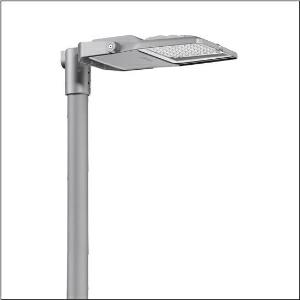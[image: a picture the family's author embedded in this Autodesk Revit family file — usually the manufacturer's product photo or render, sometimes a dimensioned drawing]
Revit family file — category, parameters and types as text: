
# Revit family: floodlight_fl_21_iq_mini___pl52_5xa7771d4d3a_bc98
name_source: partatom
category: Lighting Fixtures
units: mm (PartAtom-declared; Revit-internal decimal feet)

## family parameters
Cut with Voids When Loaded = No
Host = Face
Light Source = No
Part Type = Normal
Room Calculation Point = No
Round Connector Dimension = Use Diameter
Shared = No

## types (1)
- --- (1 x LED, 18610 lm, 143 W, 4000K)
    Apparent Load = 143 VA
    CIE Flux Codes = 26 60 98 100 100
    Color Rendering = 70
    Color Temperature = 4000K
    Default Elevation = 1800 mm
    Description = Floodlight FL 21 iQ mini, floodlight, primary light control with lens, of PMMA, primary optical cover: protective disc, of toughened safety glass, transparent, light distribution: PL52, light emission: direct distribution, installation type: surface-mounted, LED, High Power LED, rated luminous flux: 18.610lm, luminous efficacy: 130lm/W, light colour: 740, colour temperature: 4000K, control: Auto-Match, Temp-Guard, Lumen-Switch, Night-Set, Smart-Wire, Light-Fading, Desk-Remote (wireless, voltage-free reading and setting of iQ features in the workshop via application-optimized NFC function/RFID function), optimised constant luminous flux control (CLO 2.0), with terminal, 6-pole, mains connection: 220..240V, AC, 50/60Hz, start of lifetime: 143W, end of service life: 152W, reduction: 61W, luminaire housing, of diecast aluminium, powder-coated, Siteco® metallic grey (DB 702S), corrosivity category C5 mid according to DIN EN ISO 12944, sealing non-destructively replaceable, please order mast flange separately, mast bracket, of steel, galvanised, powder-coated, Siteco® metallic grey (DB 702S), protection rating (complete): IP66, insulation class (complete): insulation class II (safety insulation), certification: CE, ENEC, VDE, protection symbol: D, impact resistance: IK08, permissible operating ambient temperature: -40..+40°C, permissible operating ambient temperature for outdoor applications: -40..+50°C, standard: DIN EN 12944, LABS conformity tested according to VDMA 24364:2018-05, packaging unit: 1 piece

Light Distribution: PL52
    Height = 70 mm
    Lamp = 1 x LED
    Lamp Light Flux = 18610 lm
    Lamp Power = 143 W
    Lamp count = 1
    Length = 485 mm
    Luminous efficacy = 130 lm/W
    Manufacturer = Siteco
    ModVariant = No
    Model = 5XA7771D4D3A
    Number of Poles = 1
    OnlyDefault = Yes
    Power Factor = 1
    Product Name = Floodlight FL 21 iQ mini | PL52
    Product group = floodlight | pylon annexe
    ProductGroupID = 6200
    Protection Class = Protection class II
    Protection Degree = IP 66
    RLX_Detail_Level = 1
    RLX_Emergency_Light_Flux = 0 lm
    RLX_Emergency_Type = 0
    RLX_Emergency_Type_DB = No
    RlxData = <blob elided: 101813 chars, md5=eccb21ba>
    Socket = socket
    Standby Power = 0 W
    System Light Flux = 18610 lm
    System Power = 143 W
    Type Comments = factory setting: luminous flux: 100 % | dim-lin: 254 | 730 mA
    Type Image = l_1007125.jpg
    URL = http://relux.com
    VarID = @adj_096163
    Voltage = 0 V
    Weight = 0.00 kg
    Width = 337 mm

## geometry (parser evidence)
native form markers: Blend x4, Sweep x12
no freeform markers — native parametric forms only
